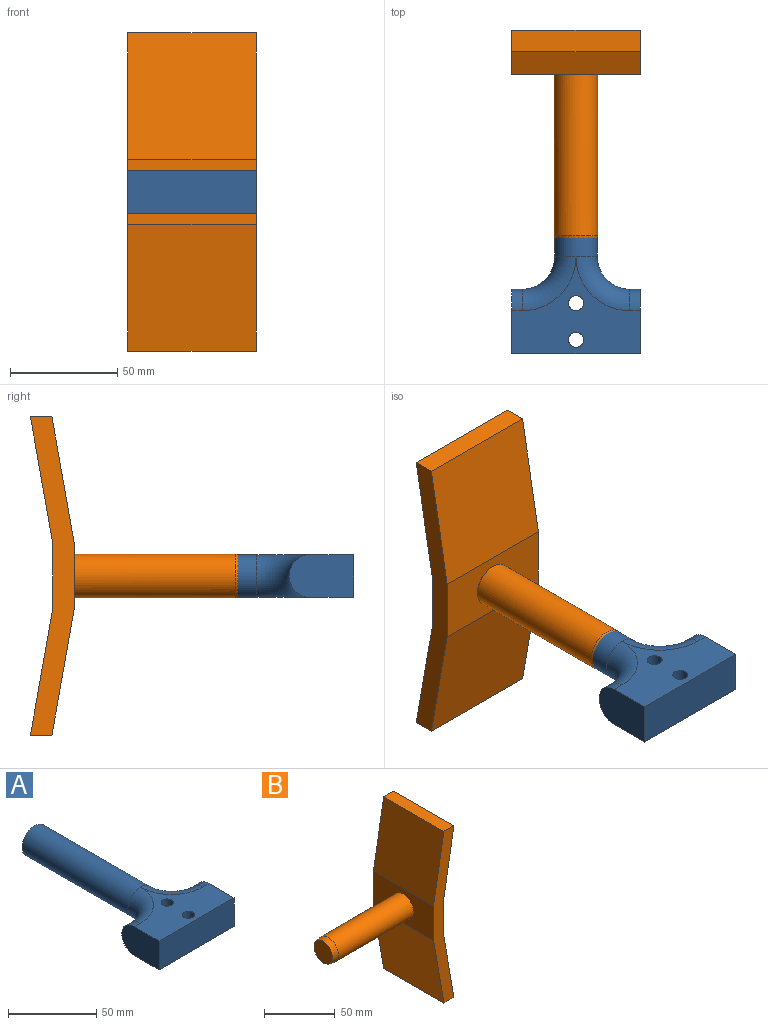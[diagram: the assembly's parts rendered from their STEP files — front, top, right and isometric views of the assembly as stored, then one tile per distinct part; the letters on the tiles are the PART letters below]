
ASSEMBLY  parts=2 mates=1
PART A: 13 faces, bbox 60x130x20 mm
  f0: plane 30x20mm, normal (-1,0,0), area 557.1mm2, adj f1,f3,f4,f10
  f1: plane 60x45mm, normal (0,0,-1), area 1391.3mm2, adj f0,f2,f4,f5,f6,f9,f10,f11
  f2: plane 30x20mm, normal (1,0,0), area 557.1mm2, adj f1,f3,f4,f12
  f3: plane 60x45mm, normal (0,0,1), area 1391.3mm2, adj f0,f2,f4,f5,f6,f9,f10,f11
  f4: plane 60x20mm, normal (0,-1,0), area 1200mm2, adj f0,f1,f2,f3
  f5: cylinder r=3.5mm len=20mm, axis (0,0,1), area 439.8mm2, adj f1,f3
  f6: cylinder r=3.5mm len=20mm, axis (0,0,1), area 439.8mm2, adj f1,f3
  f7: cylinder r=10mm len=85mm, axis (0,-1,0), area 5340.7mm2, adj f8,f9,f11
  f8: plane 20x20mm, normal (0,1,0), area 314.2mm2, adj f7
  f9: torus R=25mm, axis (0,0,1), area 919.5mm2, adj f1,f3,f7,f10
  f10: cylinder r=10mm len=20mm, axis (-1,0,0), area 157.1mm2, adj f0,f1,f3,f9
  f11: torus R=25mm, axis (0,0,1), area 919.5mm2, adj f1,f3,f7,f12
  f12: cylinder r=10mm len=20mm, axis (1,0,0), area 157.1mm2, adj f1,f2,f3,f11
PART B: 13 faces, bbox 100.4x60x148.2 mm
  f0: plane 60x59.09mm, normal (0.98,0,-0.17), area 3600mm2, adj f1,f7,f8,f9
  f1: plane 60x10mm, normal (0,0,1), area 600mm2, adj f0,f2,f8,f9
  f2: plane 60x59.09mm, normal (-0.98,0,0.17), area 3600mm2, adj f1,f3,f8,f9
  f3: plane 60x30mm, normal (-1,0,0), area 1473.1mm2, adj f2,f4,f8,f9,f10
  f4: plane 60x59.09mm, normal (-0.98,0,-0.17), area 3600mm2, adj f3,f5,f8,f9
  f5: plane 60x10mm, normal (0,0,-1), area 600mm2, adj f4,f6,f8,f9
  f6: plane 60x59.09mm, normal (0.98,0,0.17), area 3600mm2, adj f5,f7,f8,f9
  f7: plane 60x30mm, normal (1,0,0), area 1800mm2, adj f0,f6,f8,f9
  f8: plane 148.18x20.42mm, normal (0,-1,0), area 1481.8mm2, adj f0,f1,f2,f3,f4,f5,f6,f7
  f9: plane 148.18x20.42mm, normal (0,1,0), area 1481.8mm2, adj f0,f1,f2,f3,f4,f5,f6,f7
  f10: cylinder r=10.2mm len=75mm, axis (1,0,0), area 4806.6mm2, adj f3,f12
  f11: plane 18.4x18.4mm, normal (-1,0,0), area 265.9mm2, adj f12
  f12: cone r=9.2mm half-angle=11.3deg, axis (1,0,0), area 310.8mm2, adj f10,f11
PLACE A t=(-32.87,12.92,-2.18)mm
PLACE B rot(axis=(0,0,1),90deg) t=(-62.87,117.92,-2.18)mm
MATE fastened B.f10 <-> A.f7  axis (0,-1,0) through (-32.87,112.92,-2.18)mm
